# Revit family: Sanitary-Hand-&-Hair-Dryers-Sloan-Valve-EHD-701_
name_source: partatom
category: Specialty Equipment
units: mm (PartAtom-declared; Revit-internal decimal feet)

## family parameters
Cut with Voids When Loaded = No
Host = Face
OmniClass Number = 23.40.20.21.14
OmniClass Title = Hand and Hair Dryers
Part Type = Normal
Room Calculation Point = No
Round Connector Dimension = Use Diameter
Shared = No

## types (2) — shared parameters
Apparent Load = 840 VA
Assembly Code = C1030200
Connector Description = Electrical Connection
Current = 7 A
Default Elevation = 0"
Depth = 4"
Description = Sloan Optima® Air Sensor-Operated Wall - Surface - ADA Hand Dryer EHD-701 110/120V, Sloan Optima® Air Sensor-Operated Wall - Surface - ADA Hand Dryer.
Edition number = 1
Height = 13 15/16"
Keynote = 15410
Manufacturer = Sloan Valve
Number of Poles = 1
Power Factor = 1
Product data url = https://bimobject.com
URL = www.sloanvalve.com
Voltage = 120 V
Width = 8 29/32"

## per-type parameters (varying)
| type | Part Number | Product Material |
| EHD-701-BN | 3366129 | Sloan Valve - Finish - Brushed Nickel |
| EHD-701-PW | 3366128 | Sloan Valve - Finish - Polished White |

note: column(s) folded — value = type name in every type: Model

## geometry (parser evidence)
native form markers: Sweep x3
no freeform markers — native parametric forms only
